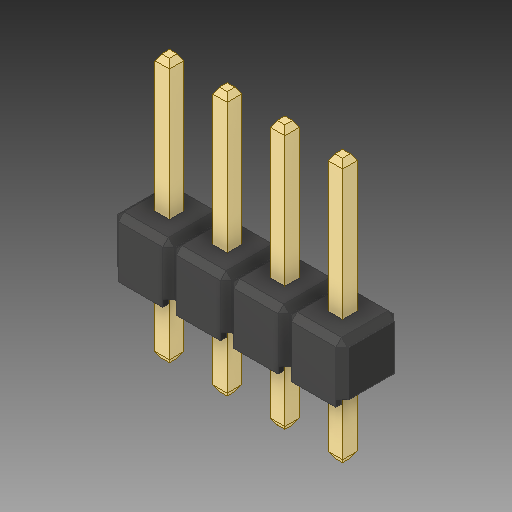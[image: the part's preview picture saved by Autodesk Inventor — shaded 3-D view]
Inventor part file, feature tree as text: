
AUTODESK INVENTOR PART (.ipt)
format: ipt  version: 2019 (Build 230136000, 136)  size: 213,504 bytes
history: native  units: in
note: dims shown in document units (in); Inventor stores cm internally (conversion verified against a paired STEP export)
features: other x7, chamfer x1
ambient origin geometry x8: Origin, YZ Plane, XZ Plane, XY Plane, X Axis, Y Axis, Z Axis, Center Point
bodies: Solid1 (feature_tree), Solid2 (feature_tree), Solid3 (feature_tree), Solid4 (feature_tree), Solid5 (feature_tree), Solid6 (feature_tree), Solid7 (feature_tree), Solid8 (feature_tree)
feature tree (8):
  chamfer  "Chamfer2"  [1 undecoded]
  other  "Boss-Extrude3"
  other  "LPattern1[1]"
  other  "LPattern1[2]"
  other  "LPattern1[3]"
  other  "LPattern1[4]"
  other  "LPattern1[5]"
  other  "LPattern1[6]"
note: 1 required parameter value undecoded (feature->parameter linkage not recoverable at this tier; creation-order binding heuristic only, values carry confidence <= 0.55)
